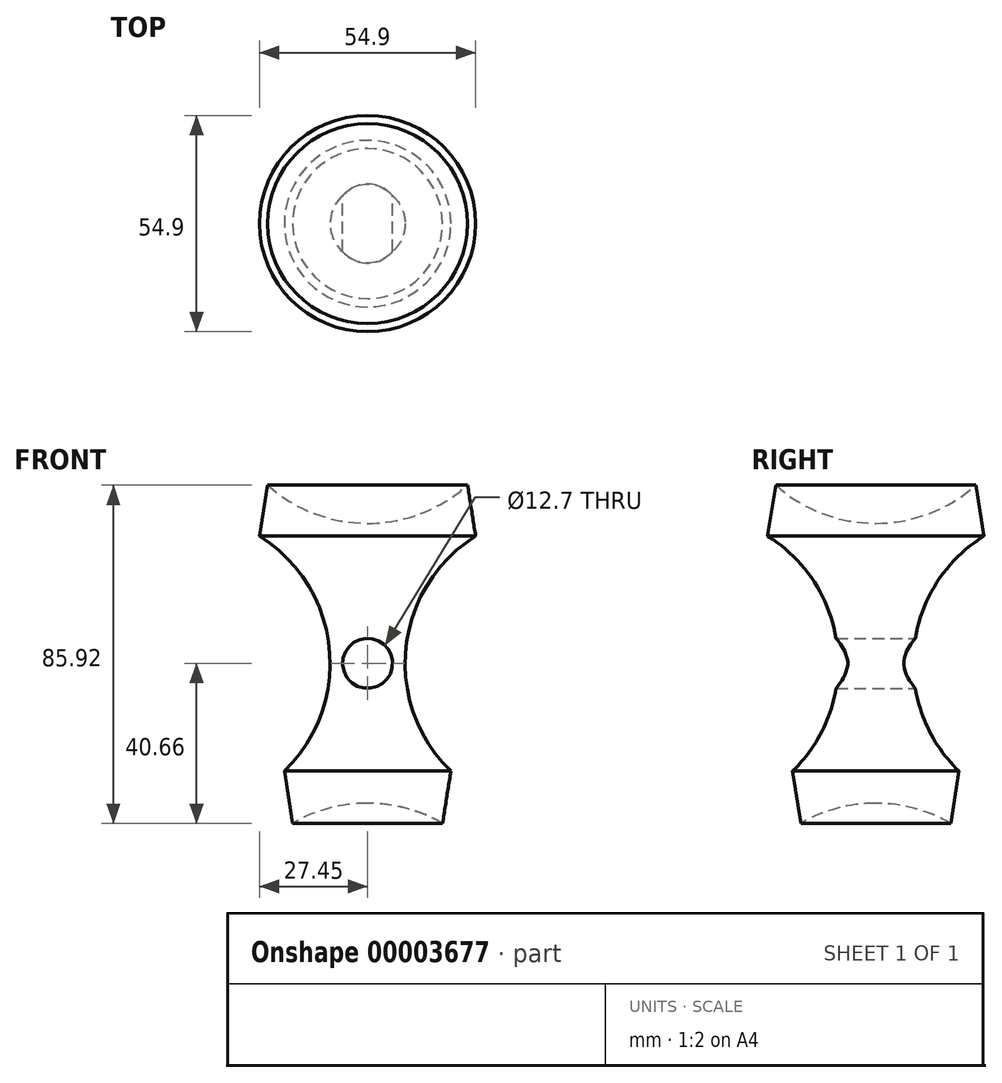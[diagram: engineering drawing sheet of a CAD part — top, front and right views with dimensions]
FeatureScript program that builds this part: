
annotation { "Feature Type Name" : "Feature", "Feature Type Description" : "" }
export const myFeature = defineFeature(function(context is Context, id is Id, definition is map)
    precondition{}
    {
        {
            var Q0;
            Q0=qCreatedBy(makeId("Front.planeOp"),FACE);
            var sketch = newSketch(context, id + "F0", { "sketchPlane" : qUnion([Q0])});
            skLineSegment(sketch, "E0", {"start": v(0, 73.66) * mm, "end": v(0, -35.56) * mm});
            skArc(sketch, "E1", {"start": v(27.45, 32.32) * mm, "mid": v(9.74, 4) * mm, "end": v(21.15, -27.4) * mm});
            skLineSegment(sketch, "E2", {"start": v(0, 0) * mm, "end": v(9.53, 0) * mm});
            skLineSegment(sketch, "E3", {"start": v(0, 0) * mm, "end": v(-9.52, 0) * mm});
            skLineSegment(sketch, "E4", {"start": v(27.45, 32.32) * mm, "end": v(25.4, 45.26) * mm});
            skArc(sketch, "E5", {"start": v(0, 35.56) * mm, "mid": v(13.6, 38.07) * mm, "end": v(25.4, 45.26) * mm});
            skPoint(sketch, "E6", {"position": v(0, 35.56) * mm});
            skArc(sketch, "E7", {"start": v(19.05, -40.66) * mm, "mid": v(9.86, -36.86) * mm, "end": v(0, -35.56) * mm});
            skLineSegment(sketch, "E8", {"start": v(21.15, -27.4) * mm, "end": v(19.05, -40.66) * mm});
            skPoint(sketch, "E9.center.orphan", {"position": v(-50.8, 0) * mm});
            skSolve(sketch);
        }
        {
            var Q0;
            {var subQ2=sQuery(id+"F0.wireOp",EDGE,"E2");Q0=makeQuery(id+"F0.imprint","IMPRINT",FACE,{"disambiguationData":[TD([[makeQuery(id+"F0.imprint","IMPRINT",EDGE,{"derivedFrom":subQ2}),-1.0]])]});}
            var Q1;
            {var subQ2=sQuery(id+"F0.wireOp",EDGE,"E2");Q1=makeQuery(id+"F0.imprint","IMPRINT",FACE,{"disambiguationData":[TD([[makeQuery(id+"F0.imprint","IMPRINT",EDGE,{"derivedFrom":subQ2}),1.0]])]});}
            var Q2;
            Q2=sQuery(id+"F0.wireOp",EDGE,"E0");
            revolve(context, id + "F1", {"entities" : qUnion([Q0, Q1]), "axis" : qUnion([Q2]), "revolveType" : RevolveType.FULL});
        }
        {
            var Q0;
            Q0=qCreatedBy(makeId("Front.planeOp"),FACE);
            var sketch = newSketch(context, id + "F2", { "sketchPlane" : qUnion([Q0])});
            skCircle(sketch, "E10", {"center": v(0, 0) * mm, "radius": 6.35 * mm});
            skSolve(sketch);
        }
        {
            var Q0;
            Q0 = qSketchRegion(id + "F2", true);
            extrude(context, id + "F3", {"entities" : qUnion([Q0]), "operationType" : NewBodyOperationType.REMOVE, "endBound" : BoundingType.THROUGH_ALL, "depth" : 25.4 * mm});
        }
        {
            var Q0;
            Q0 = qSketchRegion(id + "F2", true);
            extrude(context, id + "F4", {"entities" : qUnion([Q0]), "operationType" : NewBodyOperationType.REMOVE, "endBound" : BoundingType.THROUGH_ALL, "oppositeDirection" : true, "depth" : 25.4 * mm});
        }
    });
